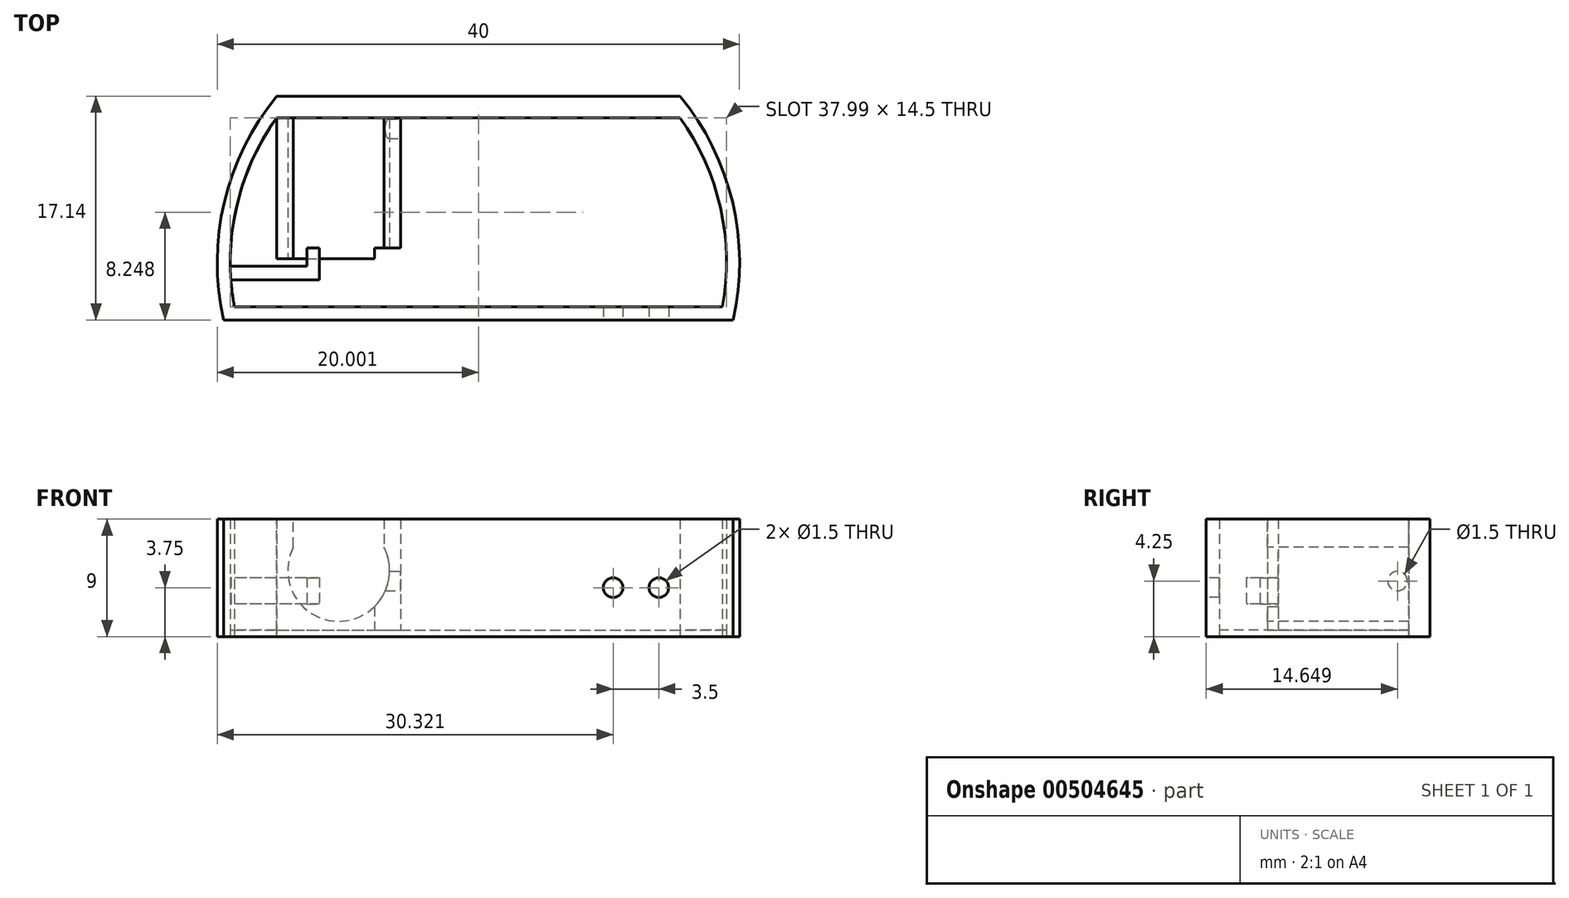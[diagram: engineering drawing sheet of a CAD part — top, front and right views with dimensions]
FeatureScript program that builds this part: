
annotation { "Feature Type Name" : "Feature", "Feature Type Description" : "" }
export const myFeature = defineFeature(function(context is Context, id is Id, definition is map)
    precondition{}
    {
        {
            var Q0;
            Q0=qCreatedBy(makeId("Top.planeOp"),FACE);
            var sketch = newSketch(context, id + "F0", { "sketchPlane" : qUnion([Q0])});
            skLineSegment(sketch, "E0.bottom", {"start": v(-8.84, 3.56) * mm, "end": v(-18.34, 3.56) * mm});
            skLineSegment(sketch, "E0.top", {"start": v(-8.84, 11.06) * mm, "end": v(-18.34, 11.06) * mm});
            skLineSegment(sketch, "E0.left", {"start": v(-8.84, 3.56) * mm, "end": v(-8.84, 11.06) * mm});
            skLineSegment(sketch, "E0.right", {"start": v(-18.34, 3.56) * mm, "end": v(-18.34, 11.06) * mm});
            skCircle(sketch, "E1", {"center": v(-2.89, 0) * mm, "radius": 19 * mm});
            skCircle(sketch, "E2", {"center": v(-2.89, 0) * mm, "radius": 20 * mm});
            skLineSegment(sketch, "E3", {"start": v(-18.34, 11.06) * mm, "end": v(12.56, 11.06) * mm});
            skLineSegment(sketch, "E4", {"start": v(-18.34, 12.7) * mm, "end": v(12.56, 12.7) * mm});
            skLineSegment(sketch, "E5", {"start": v(-21.57, -3.44) * mm, "end": v(15.8, -3.44) * mm});
            skLineSegment(sketch, "E6", {"start": v(-22.39, -4.44) * mm, "end": v(16.61, -4.44) * mm});
            skSolve(sketch);
        }
        {
            var Q0;
            Q0=makeQuery(id+"F0.imprint","IMPRINT",FACE,{"disambiguationData":[TD([[makeQuery(id+"F0.imprint","IMPRINT",EDGE,{"derivedFrom":sQuery(id+"F0.wireOp",EDGE,"E0.bottom")}),-1.0]])]});
            extrude(context, id + "F1", {"entities" : qUnion([Q0]), "depth" : 9 * mm, "offsetDistance" : 25 * mm});
        }
        {
            var Q0;
            Q0=makeQuery(id+"F1.opExtrude","SWEPT_FACE",FACE,{"disambiguationData":[OSD([sQuery(id+"F0.wireOp",EDGE,"E0.bottom"),sQuery(id+"F0.wireOp",EDGE,"L5dHV5yC-DUSC-4Zyi-QPyt-GKUG1VIBqFWS")])]});
            var sketch = newSketch(context, id + "F2", { "sketchPlane" : qUnion([Q0])});
            skCircle(sketch, "E7", {"center": v(-13.59, 5.07) * mm, "radius": 3.9 * mm});
            skPoint(sketch, "E7.centerSnap0", {"position": v(-18.34, 5.07) * mm});
            skPoint(sketch, "E7.centerSnap1", {"position": v(-13.59, 0) * mm});
            skSolve(sketch);
        }
        {
            var Q0;
            Q0=makeQuery(id+"F2.imprint","IMPRINT",FACE,{"disambiguationData":[TD([[makeQuery(id+"F2.imprint","IMPRINT",EDGE,{"derivedFrom":sQuery(id+"F2.wireOp",EDGE,"E7")}),1.0]])]});
            extrude(context, id + "F3", {"entities" : qUnion([Q0]), "operationType" : NewBodyOperationType.REMOVE, "oppositeDirection" : true, "depth" : 7.5 * mm, "offsetDistance" : 25 * mm});
        }
        {
            var Q0;
            Q0=makeQuery(id+"F1.opExtrude","SWEPT_FACE",FACE,{"disambiguationData":[OSD([sQuery(id+"F0.wireOp",EDGE,"E0.bottom"),sQuery(id+"F0.wireOp",EDGE,"L5dHV5yC-DUSC-4Zyi-QPyt-GKUG1VIBqFWS")])]});
            var sketch = newSketch(context, id + "F4", { "sketchPlane" : qUnion([Q0])});
            skLineSegment(sketch, "E8", {"start": v(-17.06, 6.86) * mm, "end": v(-17.06, 9) * mm});
            skLineSegment(sketch, "E9", {"start": v(-10.12, 6.86) * mm, "end": v(-10.12, 9) * mm});
            skSolve(sketch);
        }
        {
            var Q0;
            {var subQ0=sQuery(id+"F4.wireOp",EDGE,"E8");Q0=makeQuery(id+"F4.imprint","IMPRINT",FACE,{"disambiguationData":[TD([[makeQuery(id+"F4.imprint","IMPRINT",EDGE,{"derivedFrom":subQ0}),-1.0]])]});}
            extrude(context, id + "F5", {"entities" : qUnion([Q0]), "operationType" : NewBodyOperationType.REMOVE, "oppositeDirection" : true, "depth" : 7.5 * mm, "offsetDistance" : 25 * mm});
        }
        {
            var Q0;
            Q0=makeQuery(id+"F1.opExtrude","SWEPT_FACE",FACE,{"disambiguationData":[OSD([sQuery(id+"F0.wireOp",EDGE,"E0.left")])]});
            var sketch = newSketch(context, id + "F6", { "sketchPlane" : qUnion([Q0])});
            skCircle(sketch, "E10", {"center": v(10.2, 4.25) * mm, "radius": 0.75 * mm});
            skSolve(sketch);
        }
        {
            var Q0;
            Q0=makeQuery(id+"F6.imprint","IMPRINT",FACE,{"disambiguationData":[TD([[makeQuery(id+"F6.imprint","IMPRINT",EDGE,{"derivedFrom":sQuery(id+"F6.wireOp",EDGE,"VBwuRtHL-R972-GNgk-pwnh-6U8F89EB6MSB.bottom")}),-1.0]])]});
            var Q1;
            Q1=makeQuery(id+"F6.imprint","IMPRINT",FACE,{"disambiguationData":[TD([[makeQuery(id+"F6.imprint","IMPRINT",EDGE,{"derivedFrom":sQuery(id+"F6.wireOp",EDGE,"E10")}),1.0]])]});
            extrude(context, id + "F7", {"entities" : qUnion([Q0, Q1]), "operationType" : NewBodyOperationType.REMOVE, "oppositeDirection" : true, "depth" : 5 * mm, "offsetDistance" : 25 * mm});
        }
        {
            var Q0;
            {var subQ1=sQuery(id+"F0.wireOp",EDGE,"E0.bottom");Q0=makeQuery(id+"F0.imprint","IMPRINT",FACE,{"disambiguationData":[TD([[makeQuery(id+"F0.imprint","IMPRINT",EDGE,{"derivedFrom":subQ1}),1.0]])]});}
            extrude(context, id + "F8", {"entities" : qUnion([Q0]), "depth" : .5 * mm, "offsetDistance" : 25 * mm});
        }
        {
            var Q0;
            {var subQ5=sQuery(id+"F0.wireOp",EDGE,"E1");var subQ6=makeQuery(id+"F0.imprint","INTERSECT",VERTEX,{"disambiguationData":[OD(0.0)],"derivedFrom":[subQ5,sQuery(id+"F0.wireOp",EDGE,"E5")]});Q0=makeQuery(id+"F0.imprint","IMPRINT",FACE,{"disambiguationData":[TD([[makeQuery(id+"F0.imprint","IMPRINT",EDGE,{"disambiguationData":[TD([[subQ6,-1.0]])],"derivedFrom":subQ5}),-1.0]])]});}
            var Q1;
            {var subQ0=sQuery(id+"F0.wireOp",EDGE,"E3");var subQ2=sQuery(id+"F0.wireOp",EDGE,"E1");var subQ3=makeQuery(id+"F0.imprint","INTERSECT",VERTEX,{"derivedFrom":[subQ2,subQ0]});Q1=makeQuery(id+"F0.imprint","IMPRINT",FACE,{"disambiguationData":[TD([[makeQuery(id+"F0.imprint","IMPRINT",EDGE,{"disambiguationData":[TD([[subQ3,-1.0]])],"derivedFrom":subQ2}),1.0]])]});}
            var Q2;
            {var subQ0=sQuery(id+"F0.wireOp",EDGE,"E1");var subQ1=makeQuery(id+"F0.imprint","INTERSECT",VERTEX,{"derivedFrom":[subQ0,sQuery(id+"F0.wireOp",EDGE,"E3")]});Q2=makeQuery(id+"F0.imprint","IMPRINT",FACE,{"disambiguationData":[TD([[makeQuery(id+"F0.imprint","IMPRINT",EDGE,{"disambiguationData":[TD([[subQ1,-1.0]])],"derivedFrom":subQ0}),-1.0]])]});}
            var Q3;
            {var subQ0=sQuery(id+"F0.wireOp",EDGE,"E5");Q3=makeQuery(id+"F0.imprint","IMPRINT",FACE,{"disambiguationData":[TD([[makeQuery(id+"F0.imprint","IMPRINT",EDGE,{"derivedFrom":subQ0}),-1.0]])]});}
            extrude(context, id + "F9", {"entities" : qUnion([Q0, Q1, Q2, Q3]), "depth" : 9 * mm, "offsetDistance" : 25 * mm});
        }
        {
            var Q0;
            Q0=makeQuery(id+"F8.opExtrude","CAP_FACE",FACE,{"disambiguationData":[OSD([sQuery(id+"F0.wireOp",EDGE,"oRQTDxbB-eFFR-uNkA-U24B-d8vFeMsi9IDB.bottom"),sQuery(id+"F0.wireOp",EDGE,"oRQTDxbB-eFFR-uNkA-U24B-d8vFeMsi9IDB.top"),sQuery(id+"F0.wireOp",EDGE,"oRQTDxbB-eFFR-uNkA-U24B-d8vFeMsi9IDB.left"),sQuery(id+"F0.wireOp",EDGE,"oRQTDxbB-eFFR-uNkA-U24B-d8vFeMsi9IDB.right"),sQuery(id+"F0.wireOp",EDGE,"E0.bottom"),sQuery(id+"F0.wireOp",EDGE,"E0.top"),sQuery(id+"F0.wireOp",EDGE,"E0.left"),sQuery(id+"F0.wireOp",EDGE,"E0.right"),sQuery(id+"F0.wireOp",EDGE,"E1"),sQuery(id+"F0.wireOp",EDGE,"E3"),sQuery(id+"F0.wireOp",EDGE,"cLNeHWYX-6Nez-BgV6-V1Gx-DdiHVL3w8w64")])],"isStart":false});
            var sketch = newSketch(context, id + "F10", { "sketchPlane" : qUnion([Q0])});
            skArc(sketch, "E11.0", {"start": v(-18.39, 10.99) * mm, "mid": v(-21.78, 2.05) * mm, "end": v(-20.39, -7.4) * mm});
            skLineSegment(sketch, "E12", {"start": v(-21.86, -0.97) * mm, "end": v(-15.71, -0.97) * mm});
            skLineSegment(sketch, "E13", {"start": v(-15.71, -0.97) * mm, "end": v(-15.71, 0.92) * mm});
            skLineSegment(sketch, "E14", {"start": v(-15.71, 0.92) * mm, "end": v(-14.75, 0.92) * mm});
            skLineSegment(sketch, "E15", {"start": v(-14.75, 0.92) * mm, "end": v(-14.75, -2.01) * mm});
            skLineSegment(sketch, "E16", {"start": v(-14.75, -2.01) * mm, "end": v(-21.78, -2.01) * mm});
            skSolve(sketch);
        }
        {
            var Q0;
            {var subQ1=sQuery(id+"F10.wireOp",EDGE,"E12");Q0=makeQuery(id+"F10.imprint","IMPRINT",FACE,{"disambiguationData":[TD([[makeQuery(id+"F10.imprint","IMPRINT",EDGE,{"derivedFrom":subQ1}),-1.0]])]});}
            cPlane(context, id + "F11", {"entities" : qUnion([Q0]), "cplaneType" : CPlaneType.OFFSET, "offset" : 2 * mm, "width" : 150 * mm, "height" : 150 * mm});
        }
        {
            var Q0;
            Q0=qCreatedBy(id+"F11.planeOp",FACE);
            var sketch = newSketch(context, id + "F12", { "sketchPlane" : qUnion([Q0])});
            skLineSegment(sketch, "E17.1", {"start": v(-15.06, 1.57) * mm, "end": v(-15.06, -1.36) * mm});
            skLineSegment(sketch, "E17.2", {"start": v(-16.02, -0.33) * mm, "end": v(-16.02, 1.57) * mm});
            skLineSegment(sketch, "E17.3", {"start": v(-16.02, 1.57) * mm, "end": v(-15.06, 1.57) * mm});
            skLineSegment(sketch, "E18", {"start": v(-15.06, -1.36) * mm, "end": v(-22.43, -1.36) * mm});
            skLineSegment(sketch, "E19", {"start": v(-22.43, -1.36) * mm, "end": v(-22.17, -0.33) * mm});
            skLineSegment(sketch, "E20", {"start": v(-16.02, -0.33) * mm, "end": v(-22.17, -0.33) * mm});
            skSolve(sketch);
        }
        {
            var Q0;
            {var subQ1=sQuery(id+"F12.wireOp",EDGE,"E17.0.0");Q0=makeQuery(id+"F12.imprint","IMPRINT",FACE,{"disambiguationData":[TD([[makeQuery(id+"F12.imprint","IMPRINT",EDGE,{"derivedFrom":subQ1}),1.0]])]});}
            var Q1;
            Q1=makeQuery(id+"F12.imprint","IMPRINT",FACE,{"disambiguationData":[TD([[makeQuery(id+"F12.imprint","IMPRINT",EDGE,{"derivedFrom":sQuery(id+"F12.wireOp",EDGE,"E17.1")}),-1.0]])]});
            extrude(context, id + "F13", {"entities" : qUnion([Q0, Q1]), "operationType" : NewBodyOperationType.ADD, "depth" : 2 * mm, "offsetDistance" : 25 * mm});
        }
        {
            var Q0;
            Q0=makeQuery(id+"F9.opExtrude","SWEPT_FACE",FACE,{"disambiguationData":[OSD([sQuery(id+"F0.wireOp",EDGE,"E6")])]});
            var sketch = newSketch(context, id + "F14", { "sketchPlane" : qUnion([Q0])});
            skCircle(sketch, "E21", {"center": v(10.93, 3.75) * mm, "radius": 0.75 * mm});
            skCircle(sketch, "E22", {"center": v(7.43, 3.75) * mm, "radius": 0.75 * mm});
            skSolve(sketch);
        }
        {
            var Q0;
            Q0=makeQuery(id+"F14.imprint","IMPRINT",FACE,{"disambiguationData":[TD([[makeQuery(id+"F14.imprint","IMPRINT",EDGE,{"derivedFrom":sQuery(id+"F14.wireOp",EDGE,"E22")}),1.0]])]});
            var Q1;
            Q1=makeQuery(id+"F14.imprint","IMPRINT",FACE,{"disambiguationData":[TD([[makeQuery(id+"F14.imprint","IMPRINT",EDGE,{"derivedFrom":sQuery(id+"F14.wireOp",EDGE,"E21")}),1.0]])]});
            extrude(context, id + "F15", {"entities" : qUnion([Q0, Q1]), "operationType" : NewBodyOperationType.REMOVE, "oppositeDirection" : true, "depth" : 5 * mm, "offsetDistance" : 25 * mm});
        }
        {
            var Q0;
            Q0=makeQuery(id+"F1.opExtrude","SWEPT_FACE",FACE,{"disambiguationData":[OSD([sQuery(id+"F0.wireOp",EDGE,"E0.bottom")])]});
            extrude(context, id + "F16", {"entities" : qUnion([Q0]), "operationType" : NewBodyOperationType.ADD, "depth" : .8 * mm, "offsetDistance" : 25 * mm});
        }
        {
            var Q0;
            Q0=makeQuery(id+"F13.opExtrude","SWEPT_FACE",FACE,{"disambiguationData":[OSD([sQuery(id+"F12.wireOp",EDGE,"E17.3")])]});
            extrude(context, id + "F17", {"entities" : qUnion([Q0]), "operationType" : NewBodyOperationType.REMOVE, "oppositeDirection" : true, "depth" : .5 * mm, "offsetDistance" : 25 * mm});
        }
        {
            var Q0;
            {var subQ0=sQuery(id+"F0.wireOp",EDGE,"E0.left");Q0=makeQuery(id+"F16.boolean.opBoolean","MERGE",FACE,{"derivedFrom":[makeQuery(id+"F1.opExtrude","SWEPT_FACE",FACE,{"disambiguationData":[OSD([subQ0])]}),makeQuery(id+"F16.opExtrude","SWEPT_FACE",FACE,{"disambiguationData":[OSD([sQuery(id+"F0.wireOp",EDGE,"E0.bottom"),subQ0])]})]});}
            var sketch = newSketch(context, id + "F18", { "sketchPlane" : qUnion([Q0])});
            skLineSegment(sketch, "E23", {"start": v(3.58, 9) * mm, "end": v(3.58, 0.5) * mm});
            skSolve(sketch);
        }
        {
            var Q0;
            {var subQ0=sQuery(id+"F18.wireOp",EDGE,"E23");Q0=makeQuery(id+"F18.imprint","IMPRINT",FACE,{"disambiguationData":[TD([[makeQuery(id+"F18.imprint","IMPRINT",EDGE,{"derivedFrom":subQ0}),-1.0]])]});}
            extrude(context, id + "F19", {"entities" : qUnion([Q0]), "operationType" : NewBodyOperationType.REMOVE, "oppositeDirection" : true, "depth" : 2 * mm, "offsetDistance" : 25 * mm});
        }
        {
            var Q0;
            Q0=makeQuery(id+"F19.boolean.opBoolean","COPY",FACE,{"derivedFrom":makeQuery(id+"F19.opExtrude","SWEPT_FACE",FACE,{"disambiguationData":[OSD([sQuery(id+"F18.wireOp",EDGE,"E23")])]})});
            var Q1;
            Q1=makeQuery(id+"F16.opExtrude","CAP_FACE",FACE,{"disambiguationData":[OSD([sQuery(id+"F0.wireOp",EDGE,"E0.bottom")])],"isStart":false});
            extrude(context, id + "F20", {"entities" : qUnion([Q0, Q1]), "operationType" : NewBodyOperationType.ADD, "depth" : 2.5 * mm, "offsetDistance" : 25 * mm});
        }
    });
